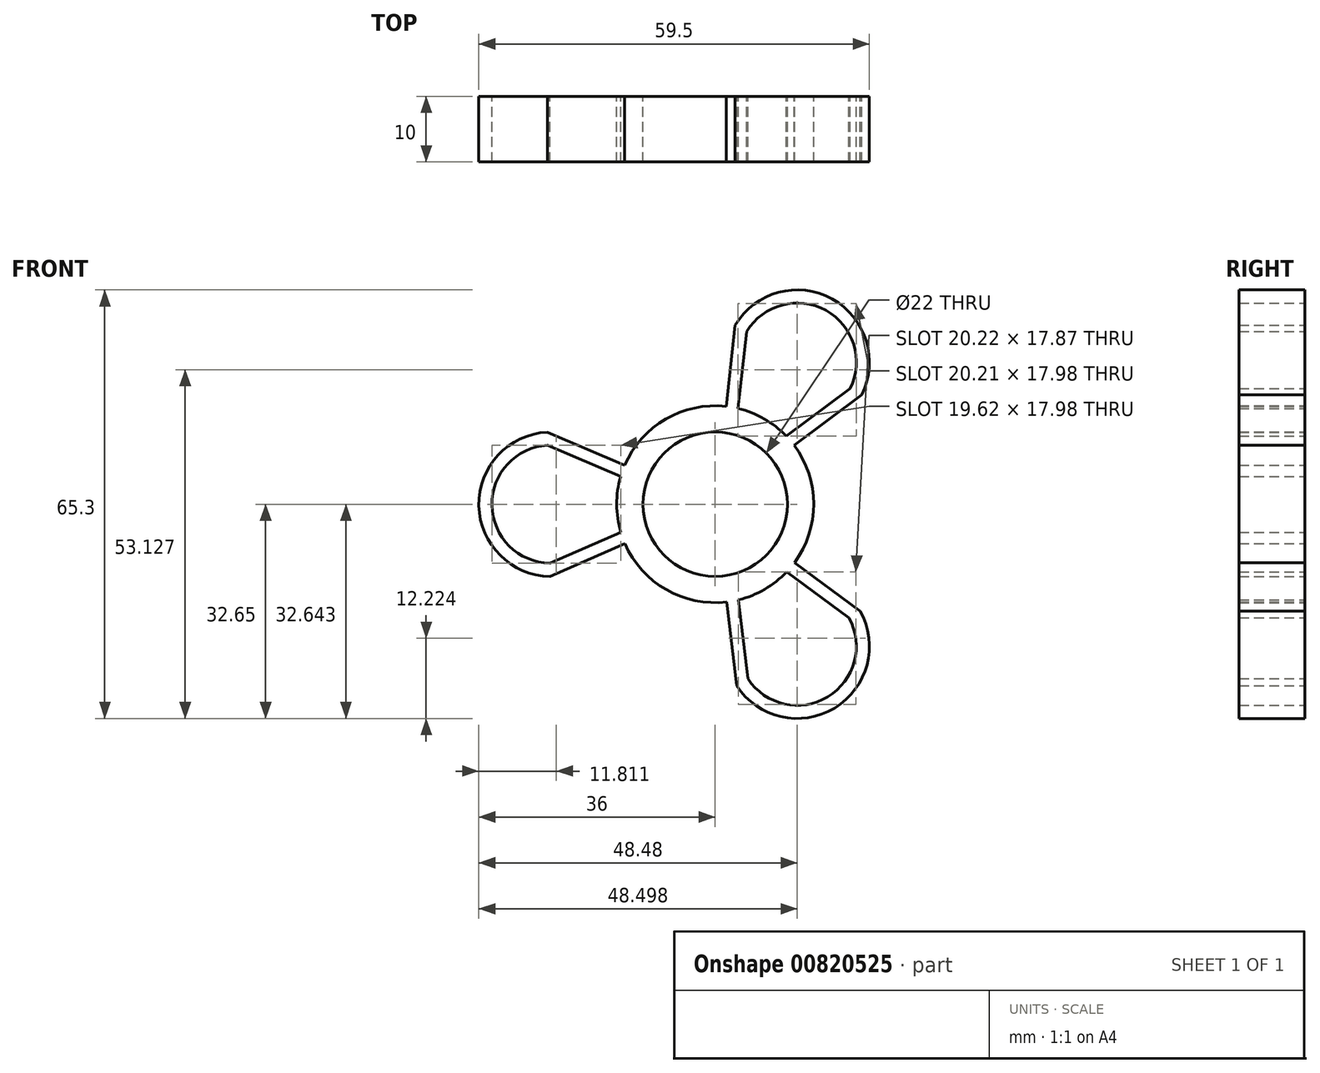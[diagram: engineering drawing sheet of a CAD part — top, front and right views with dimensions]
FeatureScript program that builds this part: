
annotation { "Feature Type Name" : "Feature", "Feature Type Description" : "" }
export const myFeature = defineFeature(function(context is Context, id is Id, definition is map)
    precondition{}
    {
        {
            var Q0;
            Q0=qCreatedBy(makeId("Front.planeOp"),FACE);
            var sketch = newSketch(context, id + "F0", { "sketchPlane" : qUnion([Q0])});
            skArc(sketch, "E0", {"start": v(-5.5, 9.53) * mm, "mid": v(-11, 0) * mm, "end": v(-5.5, -9.53) * mm});
            skArc(sketch, "E1", {"start": v(-14.4, 4.2) * mm, "mid": v(-15, -0.04) * mm, "end": v(-14.38, -4.27) * mm});
            skArc(sketch, "E2", {"start": v(-25.57, 10.99) * mm, "mid": v(-36, -0.21) * mm, "end": v(-25.15, -11) * mm});
            skLineSegment(sketch, "E3", {"start": v(-25.57, 10.99) * mm, "end": v(-13.78, 5.92) * mm});
            skLineSegment(sketch, "E4", {"start": v(-25.15, -11) * mm, "end": v(-13.74, -6.01) * mm});
            skArc(sketch, "E5", {"start": v(-25.53, 8.98) * mm, "mid": v(-34, -0.17) * mm, "end": v(-25.19, -9) * mm});
            skLineSegment(sketch, "E6", {"start": v(-25.53, 8.98) * mm, "end": v(-14.4, 4.2) * mm});
            skLineSegment(sketch, "E7", {"start": v(-25.19, -9) * mm, "end": v(-14.38, -4.27) * mm});
            skArc(sketch, "E8.trimOffspring", {"start": v(-13.74, -6.01) * mm, "mid": v(-11.18, -10) * mm, "end": v(-7.5, -13) * mm});
            skArc(sketch, "E9.trimOffspring", {"start": v(-7.5, 13) * mm, "mid": v(-11.21, 9.96) * mm, "end": v(-13.78, 5.92) * mm});
            skArc(sketch, "E10.1.0", {"start": v(-5.5, -9.53) * mm, "mid": v(5.5, -9.53) * mm, "end": v(11, 0) * mm});
            skLineSegment(sketch, "E10.1.1", {"start": v(20.39, -17.31) * mm, "end": v(10.89, -10.32) * mm});
            skArc(sketch, "E10.1.2", {"start": v(4.99, -26.6) * mm, "mid": v(17.15, -29.36) * mm, "end": v(20.39, -17.31) * mm});
            skLineSegment(sketch, "E10.1.3", {"start": v(3.27, -27.64) * mm, "end": v(1.76, -14.9) * mm});
            skArc(sketch, "E10.1.4", {"start": v(-7.5, -13) * mm, "mid": v(-3.02, -14.7) * mm, "end": v(1.76, -14.9) * mm});
            skArc(sketch, "E10.1.5", {"start": v(12.08, -8.9) * mm, "mid": v(14.25, -4.68) * mm, "end": v(15, 0) * mm});
            skLineSegment(sketch, "E10.1.6", {"start": v(4.99, -26.6) * mm, "end": v(3.56, -14.57) * mm});
            skArc(sketch, "E10.1.8", {"start": v(3.27, -27.64) * mm, "mid": v(18.18, -31.07) * mm, "end": v(22.1, -16.28) * mm});
            skLineSegment(sketch, "E10.1.9", {"start": v(22.1, -16.28) * mm, "end": v(12.08, -8.9) * mm});
            skArc(sketch, "E10.1.10", {"start": v(3.56, -14.57) * mm, "mid": v(7.53, -12.97) * mm, "end": v(10.89, -10.32) * mm});
            skArc(sketch, "E10.2.0", {"start": v(11, 0) * mm, "mid": v(5.5, 9.53) * mm, "end": v(-5.5, 9.53) * mm});
            skLineSegment(sketch, "E10.2.1", {"start": v(4.8, 26.31) * mm, "end": v(3.5, 14.59) * mm});
            skArc(sketch, "E10.2.2", {"start": v(20.55, 17.62) * mm, "mid": v(16.85, 29.53) * mm, "end": v(4.8, 26.31) * mm});
            skLineSegment(sketch, "E10.2.3", {"start": v(22.3, 16.65) * mm, "end": v(12.02, 8.98) * mm});
            skArc(sketch, "E10.2.4", {"start": v(15, 0) * mm, "mid": v(14.24, 4.73) * mm, "end": v(12.02, 8.98) * mm});
            skArc(sketch, "E10.2.5", {"start": v(1.67, 14.9) * mm, "mid": v(-3.07, 14.68) * mm, "end": v(-7.5, 13) * mm});
            skLineSegment(sketch, "E10.2.6", {"start": v(20.55, 17.62) * mm, "end": v(10.84, 10.37) * mm});
            skArc(sketch, "E10.2.8", {"start": v(22.3, 16.65) * mm, "mid": v(17.81, 31.28) * mm, "end": v(3.05, 27.28) * mm});
            skLineSegment(sketch, "E10.2.9", {"start": v(3.05, 27.28) * mm, "end": v(1.67, 14.9) * mm});
            skArc(sketch, "E10.2.10", {"start": v(10.84, 10.37) * mm, "mid": v(7.47, 13) * mm, "end": v(3.5, 14.59) * mm});
            skSolve(sketch);
        }
        {
            var Q0;
            Q0 = qSketchRegion(id + "F0", true);
            extrude(context, id + "F1", {"entities" : qUnion([Q0]), "depth" : 10 * mm, "offsetDistance" : 25 * mm});
        }
    });
